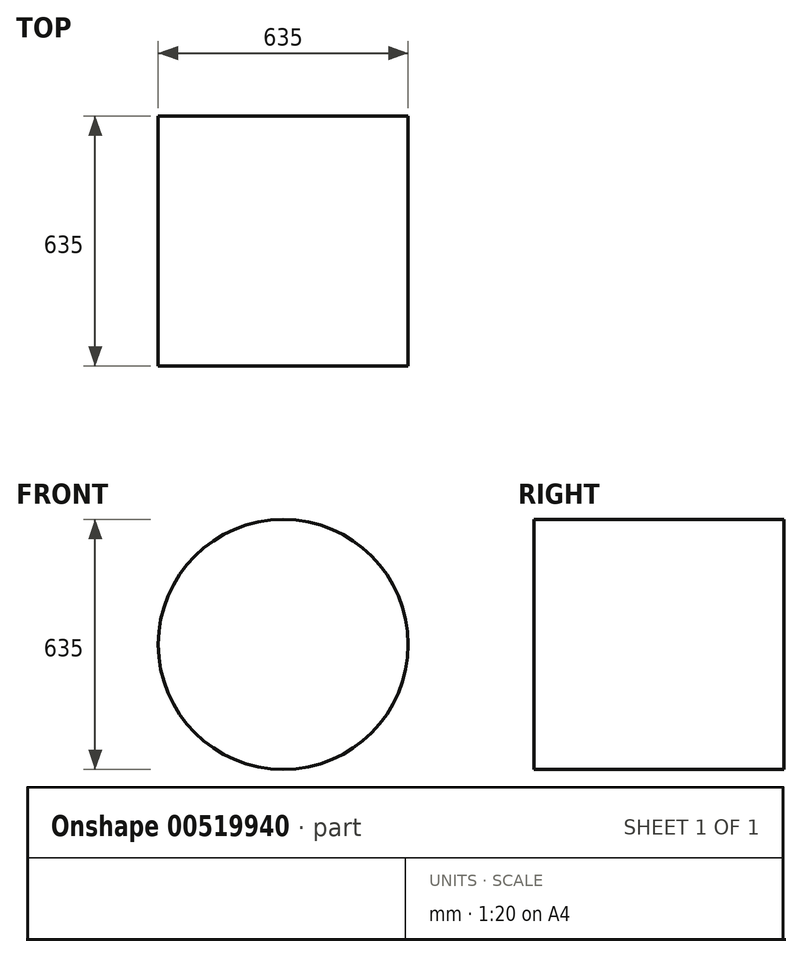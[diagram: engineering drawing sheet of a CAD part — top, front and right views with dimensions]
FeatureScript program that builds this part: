
annotation { "Feature Type Name" : "Feature", "Feature Type Description" : "" }
export const myFeature = defineFeature(function(context is Context, id is Id, definition is map)
    precondition{}
    {
        {
            var Q0;
            Q0=qCreatedBy(makeId("Front.planeOp"),FACE);
            var sketch = newSketch(context, id + "F0", { "sketchPlane" : qUnion([Q0])});
            skCircle(sketch, "E0", {"center": v(0, 0) * mm, "radius": 317.5 * mm});
            skSolve(sketch);
        }
        {
            var Q0;
            Q0=makeQuery(id+"F0.imprint","IMPRINT",FACE,{"disambiguationData":[TD([[makeQuery(id+"F0.imprint","IMPRINT",EDGE,{"derivedFrom":sQuery(id+"F0.wireOp",EDGE,"E0")}),1.0]])]});
            var Q1;
            Q1=sQuery(id+"F0.wireOp",EDGE,"E0");
            extrude(context, id + "F1", {"entities" : qUnion([Q0]), "surfaceEntities" : qUnion([Q1]), "endBound" : BoundingType.SYMMETRIC, "oppositeDirection" : true, "depth" : 635 * mm, "offsetDistance" : 25.4 * mm});
        }
    });
